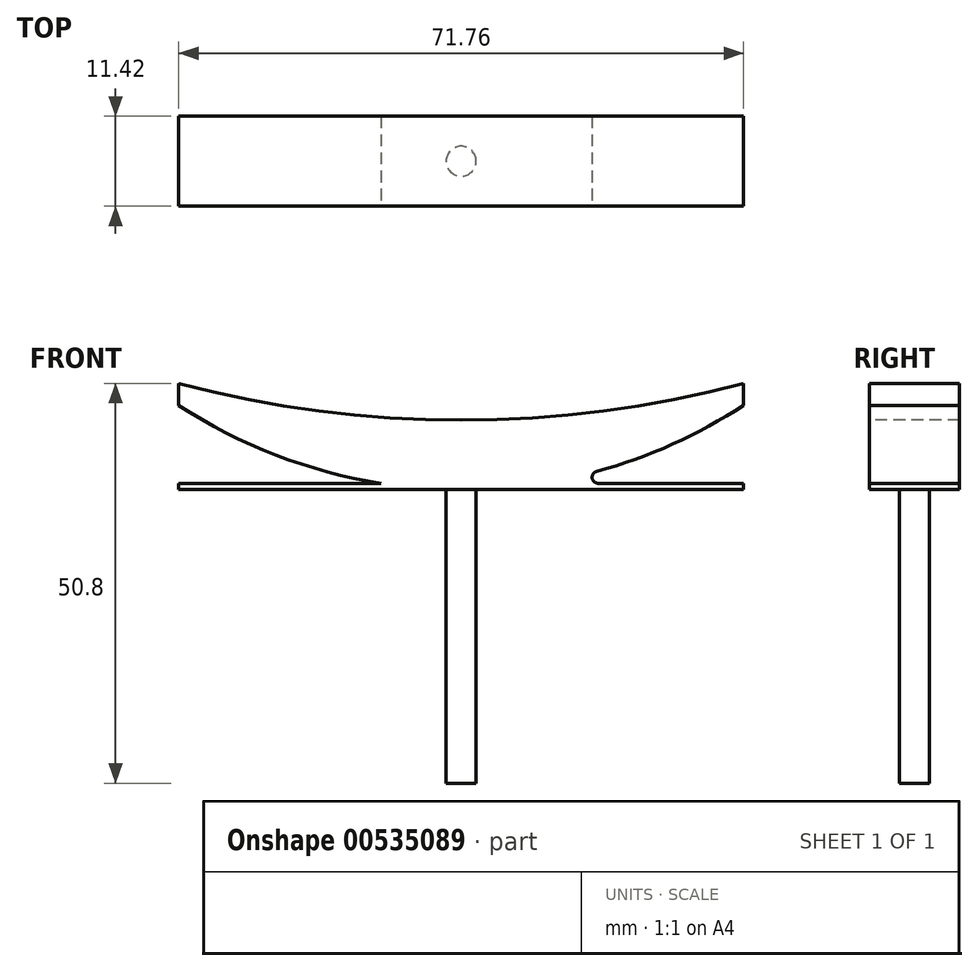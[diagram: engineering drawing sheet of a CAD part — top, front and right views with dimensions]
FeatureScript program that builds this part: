
annotation { "Feature Type Name" : "Feature", "Feature Type Description" : "" }
export const myFeature = defineFeature(function(context is Context, id is Id, definition is map)
    precondition{}
    {
        {
            var Q0;
            Q0=qCreatedBy(makeId("Top.planeOp"),FACE);
            var sketch = newSketch(context, id + "F0", { "sketchPlane" : qUnion([Q0])});
            skCircle(sketch, "E0", {"center": v(0, 0) * mm, "radius": 1.9 * mm});
            skSolve(sketch);
        }
        {
            var Q0;
            Q0=makeQuery(id+"F0.imprint","IMPRINT",FACE,{"disambiguationData":[TD([[makeQuery(id+"F0.imprint","IMPRINT",EDGE,{"derivedFrom":sQuery(id+"F0.wireOp",EDGE,"E0")}),1.0]])]});
            var Q1;
            Q1=qSketchRegion(id+"F2",true);
            extrude(context, id + "F1", {"entities" : qUnion([Q0, Q1]), "depth" : 38.1 * mm, "offsetDistance" : 25.4 * mm});
        }
        {
            var Q0;
            Q0=makeQuery(id+"F1.opExtrude","CAP_FACE",FACE,{"disambiguationData":[OSD([sQuery(id+"F0.wireOp",EDGE,"E0")])],"isStart":false});
            var sketch = newSketch(context, id + "F2", { "sketchPlane" : qUnion([Q0])});
            skLineSegment(sketch, "E1.bottom", {"start": v(35.88, 5.71) * mm, "end": v(-35.88, 5.71) * mm});
            skLineSegment(sketch, "E1.top", {"start": v(35.88, -5.72) * mm, "end": v(-35.88, -5.72) * mm});
            skLineSegment(sketch, "E1.left", {"start": v(35.88, 5.71) * mm, "end": v(35.88, -5.72) * mm});
            skLineSegment(sketch, "E1.right", {"start": v(-35.88, 5.71) * mm, "end": v(-35.88, -5.72) * mm});
            skPoint(sketch, "E1.middle", {"position": v(0, 0) * mm});
            skSolve(sketch);
        }
        {
            var Q0;
            Q0=makeQuery(id+"F2.imprint","IMPRINT",FACE,{"disambiguationData":[TD([[makeQuery(id+"F2.imprint","IMPRINT",EDGE,{"derivedFrom":sQuery(id+"F2.wireOp",EDGE,"E1.bottom")}),1.0]])]});
            var Q1;
            Q1=makeQuery(id+"F2.imprint","IMPRINT",FACE,{"disambiguationData":[TD([[makeQuery(id+"F2.imprint","IMPRINT",EDGE,{"derivedFrom":sQuery(id+"F2.wireOp",EDGE,"E1.top")}),1.0]])]});
            extrude(context, id + "F3", {"entities" : qUnion([Q0, Q1]), "operationType" : NewBodyOperationType.ADD, "oppositeDirection" : true, "depth" : 0.76 * mm, "offsetDistance" : 25.4 * mm});
        }
        {
            var Q0;
            Q0=makeQuery(id+"F3.opExtrude","SWEPT_FACE",FACE,{"disambiguationData":[OSD([sQuery(id+"F2.wireOp",EDGE,"E1.top")])]});
            var sketch = newSketch(context, id + "F4", { "sketchPlane" : qUnion([Q0])});
            skArc(sketch, "E2", {"start": v(-35.88, 50.8) * mm, "mid": v(0, 46.11) * mm, "end": v(35.88, 50.8) * mm});
            skLineSegment(sketch, "E3", {"start": v(-35.88, 50.8) * mm, "end": v(-35.88, 37.34) * mm});
            skLineSegment(sketch, "E4", {"start": v(35.88, 50.8) * mm, "end": v(35.88, 37.34) * mm});
            skLineSegment(sketch, "E5", {"start": v(0, 185.81) * mm, "end": v(0, 0) * mm});
            skCircle(sketch, "E6", {"center": v(0, 102.76) * mm, "radius": 65.46 * mm});
            skSolve(sketch);
        }
        {
            var Q0;
            Q0=makeQuery(id+"F4.imprint","IMPRINT",FACE,{"disambiguationData":[TD([[makeQuery(id+"F4.imprint","IMPRINT",EDGE,{"derivedFrom":sQuery(id+"F4.wireOp",EDGE,"E2")}),-1.0]])]});
            var Q1;
            Q1=makeQuery(id+"F3.opExtrude","SWEPT_FACE",FACE,{"disambiguationData":[OSD([sQuery(id+"F2.wireOp",EDGE,"E1.bottom")])]});
            extrude(context, id + "F5", {"entities" : qUnion([Q0]), "operationType" : NewBodyOperationType.ADD, "endBound" : BoundingType.UP_TO_SURFACE, "oppositeDirection" : true, "depth" : 25.4 * mm, "endBoundEntityFace" : qUnion([Q1]), "offsetDistance" : 25.4 * mm});
        }
        {
            var Q0;
            {var subQ0=sQuery(id+"F4.wireOp",EDGE,"E6");var subQ1=sQuery(id+"F2.wireOp",EDGE,"E1.top");Q0=makeQuery(id+"F5.opExtrude","SWEPT_EDGE",EDGE,{"disambiguationData":[OSD([subQ1,subQ0]),TDD([makeQuery(id+"F4.imprint","INTERSECT",VERTEX,{"disambiguationData":[OD(0.0)],"derivedFrom":[makeQuery(id+"F3.opExtrude","CAP_EDGE",EDGE,{"disambiguationData":[OSD([subQ1])],"isStart":true}),subQ0]})])]});}
            var Q1;
            {var subQ0=sQuery(id+"F4.wireOp",EDGE,"E6");var subQ1=sQuery(id+"F2.wireOp",EDGE,"E1.top");Q1=makeQuery(id+"F5.opExtrude","SWEPT_EDGE",EDGE,{"disambiguationData":[OSD([subQ1,subQ0]),TDD([makeQuery(id+"F4.imprint","INTERSECT",VERTEX,{"disambiguationData":[OD(1.0)],"derivedFrom":[makeQuery(id+"F3.opExtrude","CAP_EDGE",EDGE,{"disambiguationData":[OSD([subQ1])],"isStart":true}),subQ0]})])]});}
            fillet(context, id + "F6", {"entities" : qUnion([Q0, Q1]), "radius" : 0.76 * mm, "tangentPropagation" : true, "allowEdgeOverflow" : false});
        }
    });
